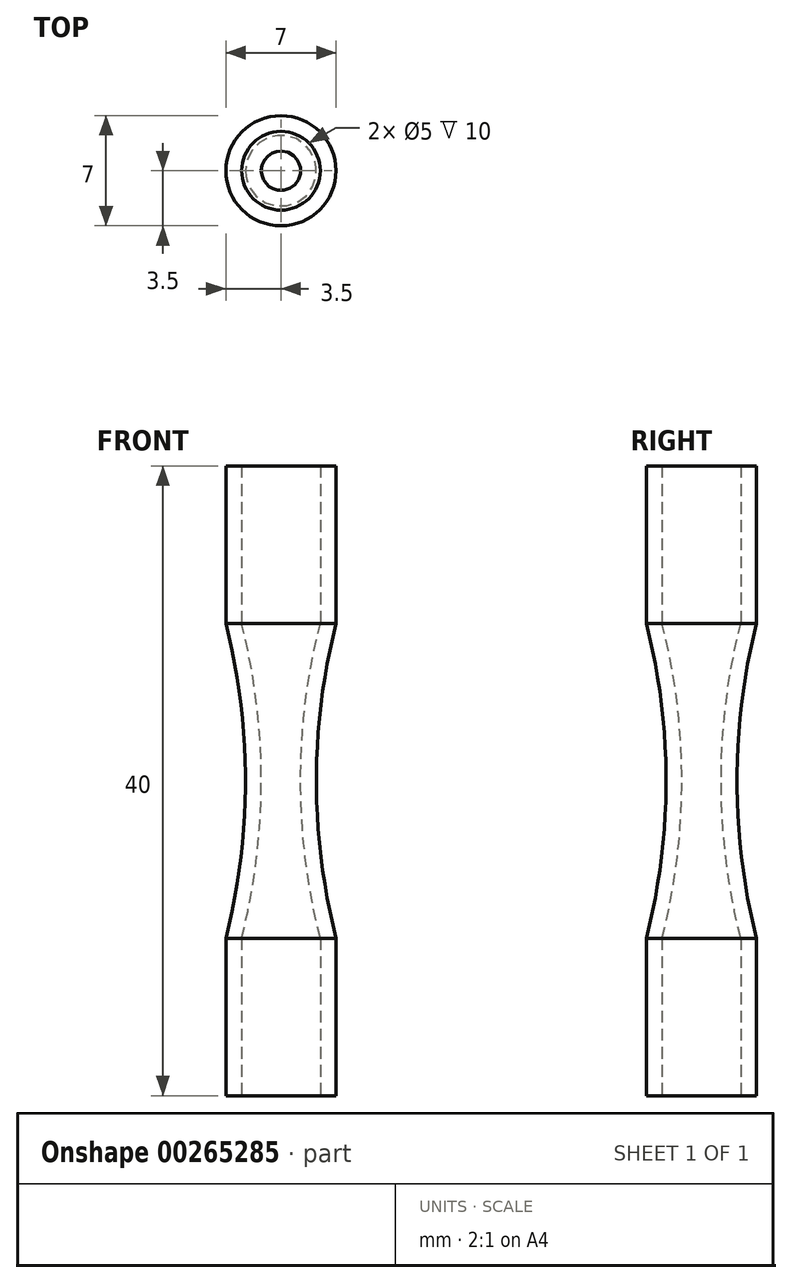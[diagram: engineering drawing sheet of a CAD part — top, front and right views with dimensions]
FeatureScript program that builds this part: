
annotation { "Feature Type Name" : "Feature", "Feature Type Description" : "" }
export const myFeature = defineFeature(function(context is Context, id is Id, definition is map)
    precondition{}
    {
        {
            var Q0;
            Q0=qCreatedBy(makeId("Front.planeOp"),FACE);
            var sketch = newSketch(context, id + "F0", { "sketchPlane" : qUnion([Q0])});
            skLineSegment(sketch, "E0", {"start": v(0, 0) * mm, "end": v(0, 40) * mm});
            skLineSegment(sketch, "E1", {"start": v(0, 0) * mm, "end": v(2.5, 0) * mm});
            skLineSegment(sketch, "E2", {"start": v(2.5, 0) * mm, "end": v(2.5, 10) * mm});
            skLineSegment(sketch, "E3", {"start": v(0, 40) * mm, "end": v(2.5, 40) * mm});
            skLineSegment(sketch, "E4", {"start": v(2.5, 40) * mm, "end": v(2.5, 30) * mm});
            skArc(sketch, "E5", {"start": v(2.5, 30) * mm, "mid": v(1.25, 20) * mm, "end": v(2.5, 10) * mm});
            skLineSegment(sketch, "E6", {"start": v(1.25, 20) * mm, "end": v(0, 20) * mm});
            skLineSegment(sketch, "E7", {"start": v(2.5, 0) * mm, "end": v(3.5, 0) * mm});
            skLineSegment(sketch, "E8", {"start": v(3.5, 0) * mm, "end": v(3.5, 10) * mm});
            skLineSegment(sketch, "E9", {"start": v(2.5, 40) * mm, "end": v(3.5, 40) * mm});
            skLineSegment(sketch, "E10", {"start": v(3.5, 40) * mm, "end": v(3.5, 30) * mm});
            skArc(sketch, "E11", {"start": v(3.5, 30) * mm, "mid": v(2.25, 20) * mm, "end": v(3.5, 10) * mm});
            skLineSegment(sketch, "E12", {"start": v(1.25, 20) * mm, "end": v(2.25, 20) * mm});
            skSolve(sketch);
        }
        {
            var Q0;
            {var subQ1=sQuery(id+"F0.wireOp",EDGE,"E2");Q0=makeQuery(id+"F0.imprint","IMPRINT",FACE,{"disambiguationData":[TD([[makeQuery(id+"F0.imprint","IMPRINT",EDGE,{"derivedFrom":subQ1}),-1.0]])]});}
            var Q1;
            {var subQ1=sQuery(id+"F0.wireOp",EDGE,"E4");Q1=makeQuery(id+"F0.imprint","IMPRINT",FACE,{"disambiguationData":[TD([[makeQuery(id+"F0.imprint","IMPRINT",EDGE,{"derivedFrom":subQ1}),1.0]])]});}
            var Q2;
            Q2=sQuery(id+"F0.wireOp",EDGE,"E0");
            revolve(context, id + "F1", {"entities" : qUnion([Q0, Q1]), "axis" : qUnion([Q2]), "revolveType" : RevolveType.FULL});
        }
    });
